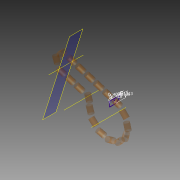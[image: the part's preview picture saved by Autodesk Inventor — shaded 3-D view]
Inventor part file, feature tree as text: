
AUTODESK INVENTOR PART (.ipt)
format: ipt  version: 2014 SP1 (Build 180222100, 222)  size: 161,792 bytes
history: native  units: mm (DEFAULTED — no unit token found)
features: other x25, extrude x20, sketch x2, plane x1, pattern_linear x1
ambient origin geometry x8: Origin, YZ Plane, XZ Plane, XY Plane, X Axis, Y Axis, Z Axis, Center Point
bodies: Body1 (feature_tree), Body2 (feature_tree), Body3 (feature_tree), Body4 (feature_tree), Body5 (feature_tree), Body6 (feature_tree), Body7 (feature_tree), Body8 (feature_tree), Body9 (feature_tree), Body10 (feature_tree), Body11 (feature_tree), Body12 (feature_tree), Body13 (feature_tree), Body14 (feature_tree), Body15 (feature_tree), Body16 (feature_tree), Body17 (feature_tree), Body18 (feature_tree), Body19 (feature_tree), Body20 (feature_tree)
feature tree (49):
  sketch  "Sketch Path"  dims[d1=10.6172mm d2=7.9375mm d3=2.682204mm d5=6.981317mm d7=0.0mm d8=0.0mm d9=0.0mm d10=0.0mm d11=7.112mm d12=0.0mm d13=200.0mm]
  other  "Cross Section Plane"
  other  "Work Axis1"
  other  "Work Axis2"
  other  "Work Axis3"
  other  "Cross Section"
  plane  "Work Plane2"
  pattern_linear  "Rectangular Pattern1"  Spacing1=7.9375mm  [1 undecoded]
  sketch  "Sketch3"  dims[d0=0.0mm]
  other  "Srf1"
  other  "Srf2"
  other  "Srf3"
  other  "Srf4"
  other  "Srf5"
  other  "Srf6"
  other  "Srf7"
  other  "Srf8"
  other  "Srf9"
  other  "Srf10"
  other  "Srf11"
  other  "Srf12"
  other  "Srf13"
  other  "Srf14"
  other  "Srf15"
  other  "Srf16"
  other  "Srf17"
  other  "Srf18"
  other  "Srf19"
  other  "Srf20"
  extrude  "ExtrusionSrf1"  Depth=2.682204mm
  extrude  "ExtrusionSrf2"  Depth=6.981317mm
  extrude  "ExtrusionSrf3"  TaperAngle=0.0deg  [1 undecoded]
  extrude  "ExtrusionSrf4"  TaperAngle=0.0deg  [1 undecoded]
  extrude  "ExtrusionSrf5"  Depth=7.112mm TaperAngle=0.0deg
  extrude  "ExtrusionSrf6"  Depth=200.0mm
  extrude  "ExtrusionSrf7"  [1 undecoded]
  extrude  "ExtrusionSrf8"  [1 undecoded]
  extrude  "ExtrusionSrf9"  [1 undecoded]
  extrude  "ExtrusionSrf10"  [1 undecoded]
  extrude  "ExtrusionSrf11"  [1 undecoded]
  extrude  "ExtrusionSrf12"  [1 undecoded]
  extrude  "ExtrusionSrf13"  [1 undecoded]
  extrude  "ExtrusionSrf14"  [1 undecoded]
  extrude  "ExtrusionSrf15"  [1 undecoded]
  extrude  "ExtrusionSrf16"  [1 undecoded]
  extrude  "ExtrusionSrf17"  [1 undecoded]
  extrude  "ExtrusionSrf18"  [1 undecoded]
  extrude  "ExtrusionSrf19"  [1 undecoded]
  extrude  "ExtrusionSrf20"  [1 undecoded]
note: 17 required parameter values undecoded (feature->parameter linkage not recoverable at this tier; creation-order binding heuristic only, values carry confidence <= 0.55)
